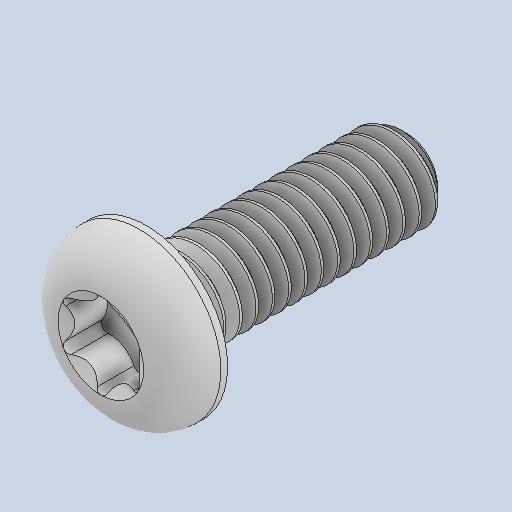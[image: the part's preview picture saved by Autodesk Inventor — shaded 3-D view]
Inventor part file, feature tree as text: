
AUTODESK INVENTOR PART (.ipt)
format: ipt  version: 2023.2 (Build 272271000, 271)  size: 658,944 bytes
history: native  units: in
note: dims shown in document units (in); Inventor stores cm internally (conversion verified against a paired STEP export)
features: extrude x1
ambient origin geometry x8: Origin, YZ Plane, XZ Plane, XY Plane, X Axis, Y Axis, Z Axis, Center Point
bodies: Solid1 (feature_tree)
feature tree (1):
  extrude  "Extrude16"  [1 undecoded]
note: 1 required parameter value undecoded (feature->parameter linkage not recoverable at this tier; creation-order binding heuristic only, values carry confidence <= 0.55)
